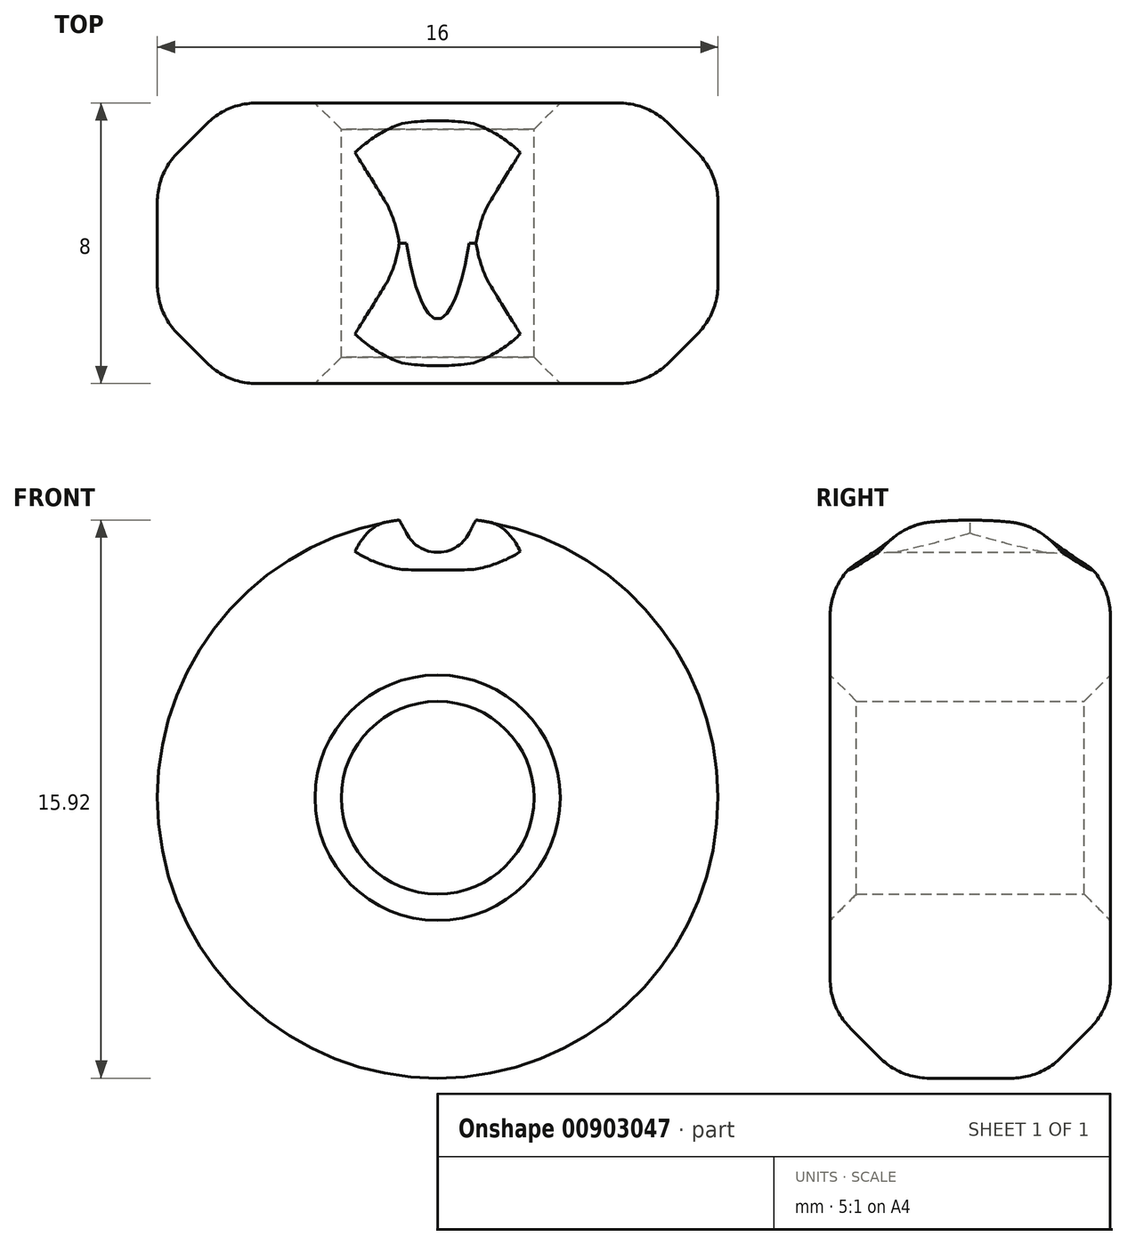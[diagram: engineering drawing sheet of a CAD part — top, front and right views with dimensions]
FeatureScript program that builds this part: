
annotation { "Feature Type Name" : "Feature", "Feature Type Description" : "" }
export const myFeature = defineFeature(function(context is Context, id is Id, definition is map)
    precondition{}
    {
        {
            var Q0;
            Q0=qCreatedBy(makeId("Front.planeOp"),FACE);
            var sketch = newSketch(context, id + "F0", { "sketchPlane" : qUnion([Q0])});
            skCircle(sketch, "E0", {"center": v(0, 0) * mm, "radius": 8 * mm});
            skCircle(sketch, "E1.0", {"center": v(0, 0) * mm, "radius": 2.75 * mm});
            skSolve(sketch);
        }
        {
            var Q0;
            Q0=qSketchRegion(id+"F0",true);
            extrude(context, id + "F1", {"entities" : qUnion([Q0]), "endBound" : BoundingType.SYMMETRIC, "depth" : 8 * mm, "offsetDistance" : 25.4 * mm});
        }
        {
            var Q0;
            Q0=makeQuery(id+"F1.opExtrude","CAP_EDGE",EDGE,{"disambiguationData":[OSD([sQuery(id+"F0.wireOp",EDGE,"E0")])],"isStart":false});
            var Q1;
            Q1=makeQuery(id+"F1.opExtrude","CAP_EDGE",EDGE,{"disambiguationData":[OSD([sQuery(id+"F0.wireOp",EDGE,"E0")])],"isStart":true});
            chamfer(context, id + "F2", {"entities" : qUnion([Q0, Q1]), "width" : 2 * mm, "tangentPropagation" : true});
        }
        {
            var Q0;
            Q0=makeQuery(id+"F1.opExtrude","CAP_FACE",FACE,{"disambiguationData":[OSD([sQuery(id+"F0.wireOp",EDGE,"E0"),sQuery(id+"F0.wireOp",EDGE,"E1.0")])],"isStart":false});
            var sketch = newSketch(context, id + "F3", { "sketchPlane" : qUnion([Q0])});
            skCircle(sketch, "E2", {"center": v(0, 8) * mm, "radius": 1 * mm});
            skSolve(sketch);
        }
        {
            var Q0;
            Q0=qSketchRegion(id+"F3",true);
            var Q1;
            Q1=makeQuery(id+"F1.opExtrude","CAP_FACE",FACE,{"disambiguationData":[OSD([sQuery(id+"F0.wireOp",EDGE,"E0"),sQuery(id+"F0.wireOp",EDGE,"E1.0")])],"isStart":true});
            var Q2;
            Q2=makeQuery(id+"F1.opExtrude","CAP_FACE",FACE,{"disambiguationData":[OSD([sQuery(id+"F0.wireOp",EDGE,"E0"),sQuery(id+"F0.wireOp",EDGE,"E1.0")])],"isStart":false});
            extrude(context, id + "F4", {"entities" : qUnion([Q0]), "operationType" : NewBodyOperationType.REMOVE, "endBound" : BoundingType.THROUGH_ALL, "oppositeDirection" : true, "depth" : 25.4 * mm, "endBoundEntityFace" : qUnion([Q1]), "offsetDistance" : 25.4 * mm});
        }
        {
            var Q0;
            Q0=makeQuery(id+"F1.opExtrude","CAP_EDGE",EDGE,{"disambiguationData":[OSD([sQuery(id+"F0.wireOp",EDGE,"E1.0")])],"isStart":false});
            var Q1;
            Q1=makeQuery(id+"F1.opExtrude","CAP_EDGE",EDGE,{"disambiguationData":[OSD([sQuery(id+"F0.wireOp",EDGE,"E1.0")])],"isStart":true});
            chamfer(context, id + "F5", {"entities" : qUnion([Q0, Q1]), "width" : .75 * mm, "tangentPropagation" : true});
        }
        {
            var Q0;
            {var subQ0=sQuery(id+"F0.wireOp",EDGE,"E0");Q0=makeQuery(id+"F2.opChamfer","BLEND_FACE",FACE,{"disambiguationData":[OSD([subQ0]),TDD([makeQuery(id+"F1.opExtrude","CAP_EDGE",EDGE,{"disambiguationData":[OSD([subQ0])],"isStart":true})])]});}
            var Q1;
            {var subQ0=sQuery(id+"F0.wireOp",EDGE,"E0");Q1=makeQuery(id+"F2.opChamfer","BLEND_FACE",FACE,{"disambiguationData":[OSD([subQ0]),TDD([makeQuery(id+"F1.opExtrude","CAP_EDGE",EDGE,{"disambiguationData":[OSD([subQ0])],"isStart":false})])]});}
            fillet(context, id + "F6", {"entities" : qUnion([Q0, Q1]), "radius" : 2 * mm, "tangentPropagation" : true, "allowEdgeOverflow" : false});
        }
    });
